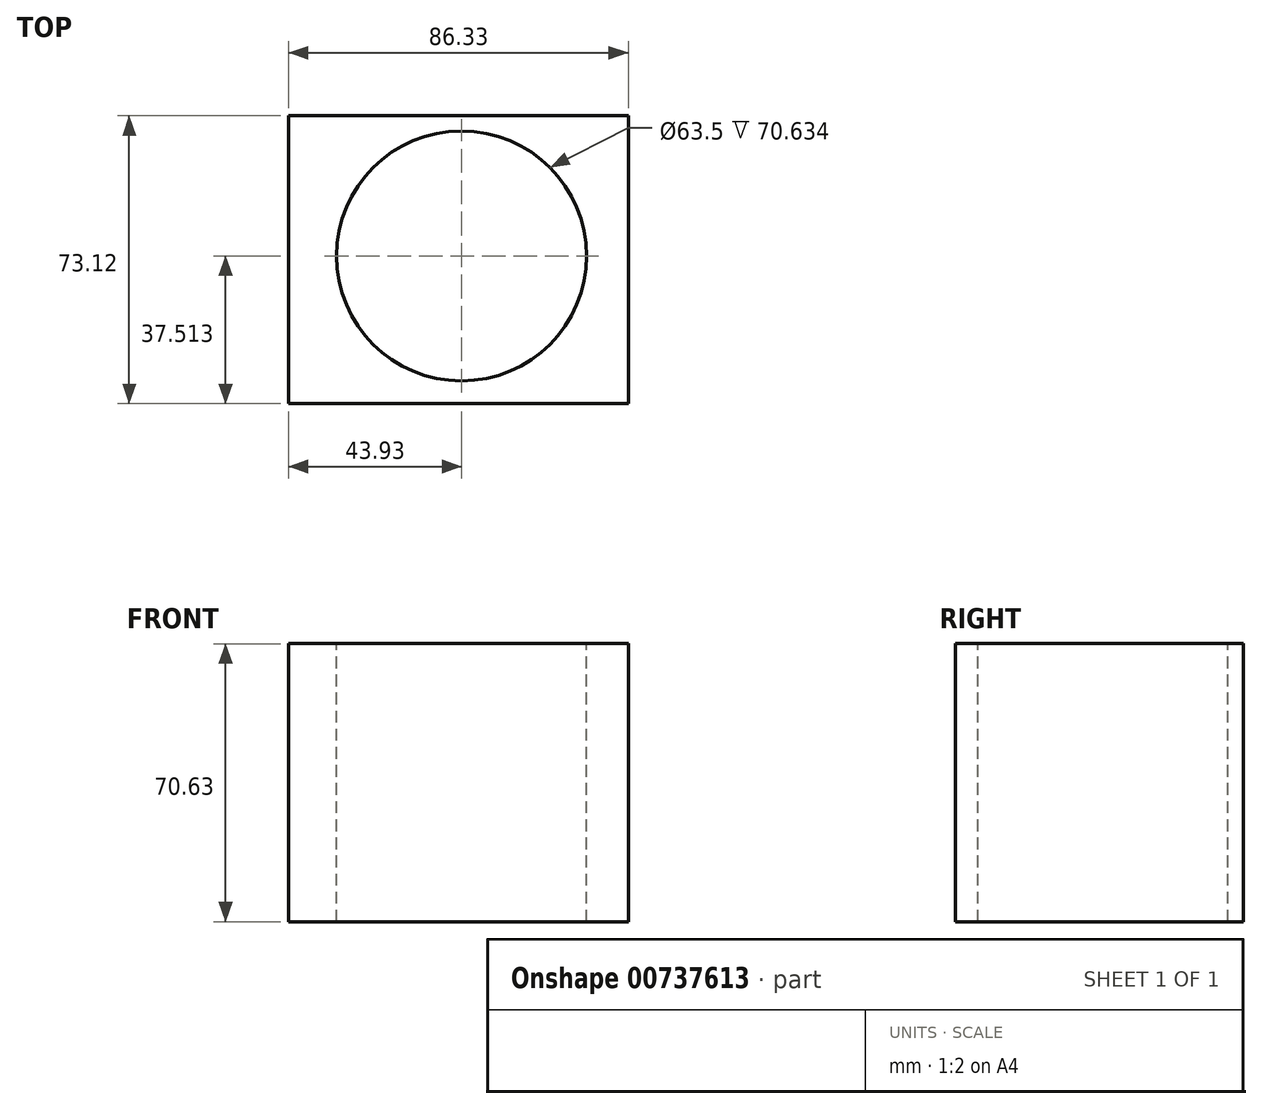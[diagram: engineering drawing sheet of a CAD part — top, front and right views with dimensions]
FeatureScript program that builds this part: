
annotation { "Feature Type Name" : "Feature", "Feature Type Description" : "" }
export const myFeature = defineFeature(function(context is Context, id is Id, definition is map)
    precondition{}
    {
        {
            var Q0;
            Q0=qCreatedBy(makeId("Top.planeOp"),FACE);
            var sketch = newSketch(context, id + "F0", { "sketchPlane" : qUnion([Q0])});
            skLineSegment(sketch, "E0.bottom", {"start": v(-43.93, 0) * mm, "end": v(42.4, 0) * mm});
            skLineSegment(sketch, "E0.top", {"start": v(-43.93, 73.12) * mm, "end": v(42.4, 73.12) * mm});
            skLineSegment(sketch, "E0.left", {"start": v(-43.93, 0) * mm, "end": v(-43.93, 73.12) * mm});
            skLineSegment(sketch, "E0.right", {"start": v(42.4, 0) * mm, "end": v(42.4, 73.12) * mm});
            skSolve(sketch);
        }
        {
            var Q0;
            Q0=makeQuery(id+"F0.imprint","IMPRINT",FACE,{"disambiguationData":[TD([[makeQuery(id+"F0.imprint","IMPRINT",EDGE,{"derivedFrom":sQuery(id+"F0.wireOp",EDGE,"E0.bottom")}),1.0]])]});
            extrude(context, id + "F1", {"entities" : qUnion([Q0]), "depth" : 70.63 * mm, "offsetDistance" : 25.4 * mm});
        }
        {
            var Q0;
            Q0=makeQuery(id+"F1.opExtrude","CAP_FACE",FACE,{"disambiguationData":[OSD([sQuery(id+"F0.wireOp",EDGE,"E0.bottom"),sQuery(id+"F0.wireOp",EDGE,"E0.top"),sQuery(id+"F0.wireOp",EDGE,"E0.left"),sQuery(id+"F0.wireOp",EDGE,"E0.right")])],"isStart":false});
            var sketch = newSketch(context, id + "F2", { "sketchPlane" : qUnion([Q0])});
            skPoint(sketch, "E1", {"position": v(0, 38.02) * mm});
            skPoint(sketch, "E2", {"position": v(-158.16, 300.93) * mm});
            skSolve(sketch);
        }
        {
            var Q0;
            Q0=makeQuery(id+"F2.imprint","IMPRINT",FACE,{"disambiguationData":[TD([[makeQuery(id+"F2.imprint","IMPRINT",EDGE,{"derivedFrom":makeQuery(id+"F1.opExtrude","CAP_EDGE",EDGE,{"disambiguationData":[OSD([sQuery(id+"F0.wireOp",EDGE,"E0.bottom")])],"isStart":false})}),1.0]])]});
            var sketch = newSketch(context, id + "F3", { "sketchPlane" : qUnion([Q0])});
            skPoint(sketch, "E3", {"position": v(0, 37.51) * mm});
            skSolve(sketch);
        }
        {
            var Q0;
            Q0=sQuery(id+"F3.wireOp",VERTEX,"E3");
            var Q1;
            Q1=makeQuery(id+"F1.opExtrude","SWEPT_BODY",BODY,{"disambiguationData":[OSD([sQuery(id+"F0.wireOp",EDGE,"E0.bottom"),sQuery(id+"F0.wireOp",EDGE,"E0.top"),sQuery(id+"F0.wireOp",EDGE,"E0.left"),sQuery(id+"F0.wireOp",EDGE,"E0.right")])]});
            hole(context, id + "F4", {"style" : HoleStyle.SIMPLE, "endStyle" : HoleEndStyle.THROUGH, "holeDiameter" : 63.5 * mm, "majorDiameter" : 6.35 * mm, "isTappedThrough" : true, "tappedDepth" : 12.7 * mm, "tapClearance" : 3, "locations" : qUnion([Q0]), "scope" : qUnion([Q1])});
        }
    });
